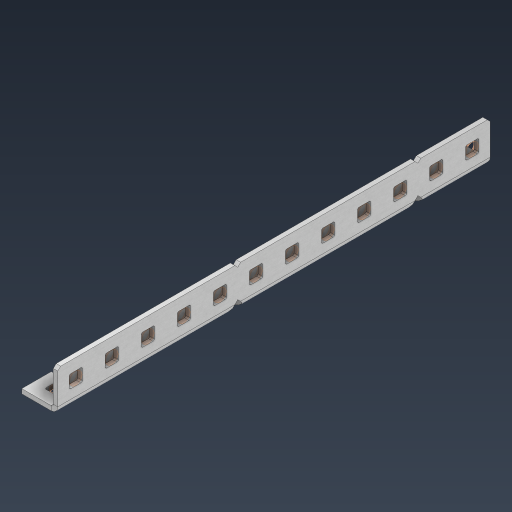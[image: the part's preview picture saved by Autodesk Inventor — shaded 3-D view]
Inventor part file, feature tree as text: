
AUTODESK INVENTOR PART (.ipt)
format: ipt  version: 2024.3 (Build 283343000, 343)  size: 653,312 bytes
history: native  units: in
note: dims shown in document units (in); Inventor stores cm internally (conversion verified against a paired STEP export)
features: other x43, extrude x34, sheet_metal_op x11, pattern_linear x2, mirror x1, chamfer x1, sketch x1
ambient origin geometry x8: Origin, YZ Plane, XZ Plane, XY Plane, X Axis, Y Axis, Z Axis, Center Point
bodies: Solid1 (feature_tree), Body (feature_tree)
feature tree (93):
  sheet_metal_op  "Flanges"
  other  "Flange Pattern Plane"
  other  "Flange Pattern Sketch"
  sheet_metal_op  "Flange Pattern"
  sheet_metal_op  "Body Pattern"
  pattern_linear  "Center Pattern"  Spacing1=6.0in  [1 undecoded]
  other  "Arc Length"
  mirror  "Notch Mirror"
  pattern_linear  "Notch Pattern"  Spacing1=0.0625in  [1 undecoded]
  chamfer  "End Chamfer"
  extrude  "Half Cut"  Depth=0.0625in
  other  "Plate1"
  sketch  "Sketch2"  dims[d0=1.0in d1=6.0in d2=0.0625in d3=0.0625in d4=0.0312in d5=0.125in d6=0.0625in d7=0.5in d8=90.0deg d9=0.0312in d10=0.25in d11=0.0625in d12=0.0625in d16=0.182in d17=0.02in d18=0.0625in d19=0.0in d20=0.25in d21=0.25in d38=4.7244in d40=0.5in d41=0.3937in d43=1.0in d46=0.172in d47=1.0in d48=0.0in d49=0.182in d50=0.02in d51=0.25in d52=0.25in d53=0.0625in d54=0.0in d55=0.172in d56=1.0in d57=0.0in d58=0.25in d60=4.7244in d62=0.5in d63=0.3937in d65=0.5in d85=0.1473in d86=0.1782in d88=0.04in d89=0.0625in d90=0.0in d91=0.04in d92=0.0491in d95=2.5in d96=0.04in d97=0.25in d98=45.0deg d99=0.25in d100=0.5in d101=0.0in d102=2.497in d106=0.182in d107=0.02in d108=0.5in d109=0.5in d110=0.0625in d111=0.0in d112=0.172in d113=0.5in d114=0.0in d117=0.5in d118=0.5in d119=0.5in]
  other  "Plate2"
  sheet_metal_op  "Bend1"
  sheet_metal_op  "Corner1"
  other  "Srf1"
  other  "Srf2"
  other  "Srf91"
  sheet_metal_op  "Body Pattern Sketch"
  other  "Srf92"
  other  "Srf786"
  other  "Srf823"
  other  "Srf824"
  other  "Srf825"
  other  "Srf826"
  other  "Srf827"
  other  "Srf828"
  other  "Srf829"
  other  "Srf856"
  other  "Srf857"
  other  "Srf858"
  other  "Srf859"
  other  "Srf860"
  other  "Srf861"
  other  "Srf862"
  other  "Srf889"
  other  "Srf890"
  other  "Srf891"
  other  "Srf892"
  other  "Srf893"
  other  "Srf894"
  other  "Srf895"
  other  "Srf896"
  other  "Srf922"
  other  "Srf923"
  other  "Srf924"
  other  "Srf959"
  other  "Srf960"
  other  "Srf961"
  other  "Srf996"
  other  "Srf997"
  other  "Srf998"
  sheet_metal_op  "Flange Stamp"
  sheet_metal_op  "Flange Circle"
  sheet_metal_op  "Body Stamp"
  sheet_metal_op  "Body Circle"
  other  "Center Stamp"
  other  "Center Circle"
  sheet_metal_op  "Notch"
  extrude  "ExtrusionSrf2"  Depth=0.0312in
  extrude  "ExtrusionSrf92"  Depth=0.5in
  extrude  "ExtrusionSrf823"  Depth=0.0625in
  extrude  "ExtrusionSrf824"  Depth=0.5in TaperAngle=90.0deg
  extrude  "ExtrusionSrf825"  Depth=0.25in
  extrude  "ExtrusionSrf826"  Depth=0.0625in
  extrude  "ExtrusionSrf827"  Depth=0.0625in
  extrude  "ExtrusionSrf828"  Depth=0.182in
  extrude  "ExtrusionSrf829"  Depth=0.02in
  extrude  "ExtrusionSrf856"  Depth=0.0625in
  extrude  "ExtrusionSrf857"  TaperAngle=0.0deg  [1 undecoded]
  extrude  "ExtrusionSrf858"  Depth=0.25in
  extrude  "ExtrusionSrf859"  Depth=0.25in
  extrude  "ExtrusionSrf860"  Depth=0.5in
  extrude  "ExtrusionSrf861"  Depth=0.5in
  extrude  "ExtrusionSrf862"  Depth=1.0in TaperAngle=0.0deg
  extrude  "ExtrusionSrf889"  Depth=0.182in
  extrude  "ExtrusionSrf890"  Depth=0.02in
  extrude  "ExtrusionSrf891"  Depth=0.25in
  extrude  "ExtrusionSrf892"  Depth=0.25in
  extrude  "ExtrusionSrf893"  Depth=0.0625in
  extrude  "ExtrusionSrf894"  TaperAngle=0.0deg  [1 undecoded]
  extrude  "ExtrusionSrf895"  Depth=0.5in
  extrude  "ExtrusionSrf896"  Depth=1.0in TaperAngle=0.0deg
  extrude  "ExtrusionSrf922"  Depth=0.25in
  extrude  "ExtrusionSrf923"  Depth=0.5in
  extrude  "ExtrusionSrf924"  Depth=0.5in
  extrude  "ExtrusionSrf959"  Depth=0.5in
  extrude  "ExtrusionSrf960"  Depth=0.5in
  extrude  "ExtrusionSrf961"  Depth=0.5in
  extrude  "ExtrusionSrf996"  Depth=0.0625in
  extrude  "ExtrusionSrf997"  TaperAngle=0.0deg  [1 undecoded]
  extrude  "ExtrusionSrf998"  Depth=0.5in
note: 5 required parameter values undecoded (feature->parameter linkage not recoverable at this tier; creation-order binding heuristic only, values carry confidence <= 0.55)
